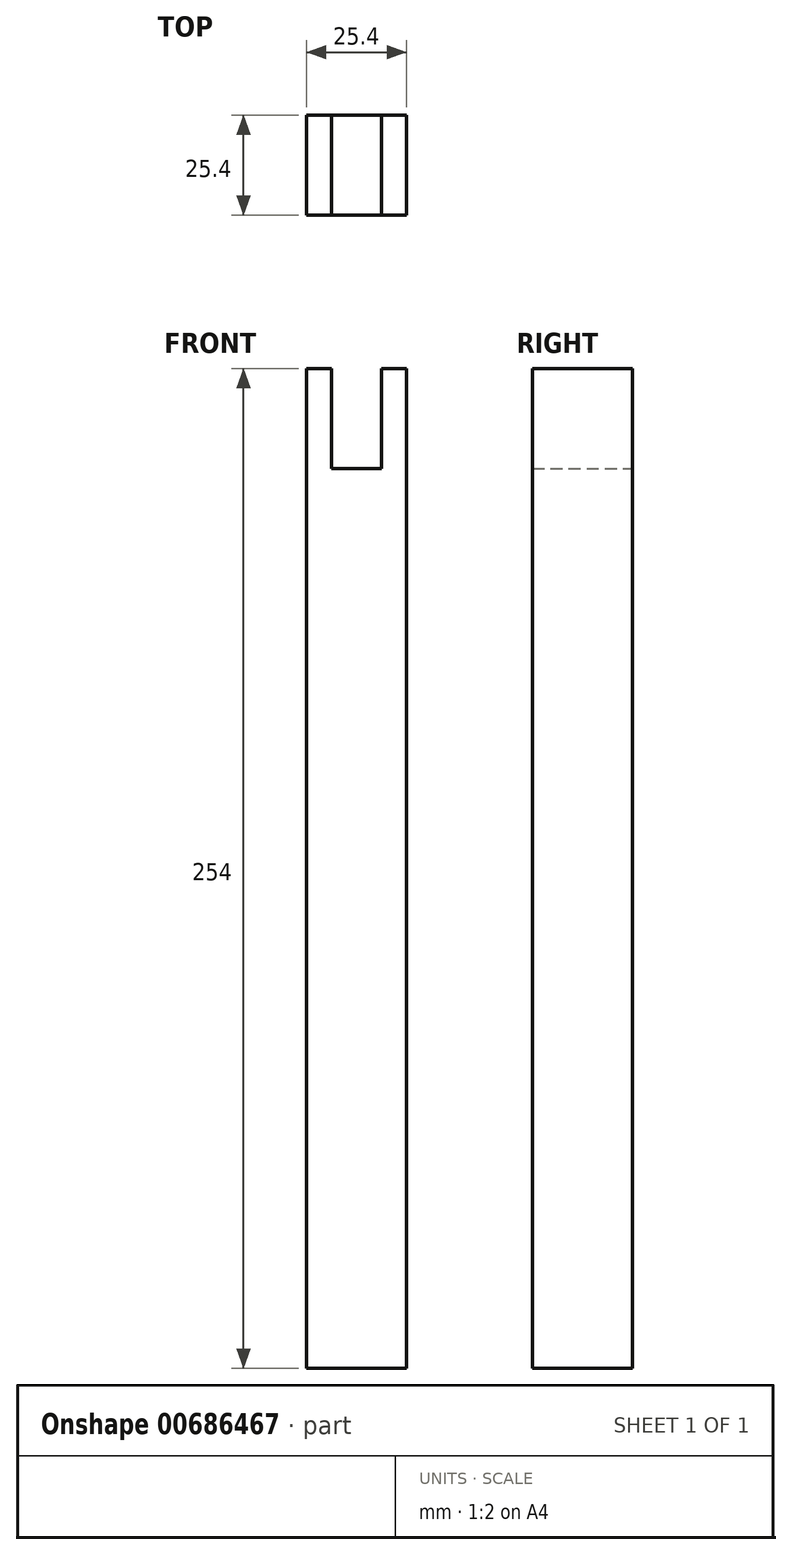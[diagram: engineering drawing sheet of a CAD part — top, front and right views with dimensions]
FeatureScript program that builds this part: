
annotation { "Feature Type Name" : "Feature", "Feature Type Description" : "" }
export const myFeature = defineFeature(function(context is Context, id is Id, definition is map)
    precondition{}
    {
        {
            var Q0;
            Q0=qCreatedBy(makeId("Front.planeOp"),FACE);
            var sketch = newSketch(context, id + "F0", { "sketchPlane" : qUnion([Q0])});
            skLineSegment(sketch, "E0.bottom", {"start": v(0, 0) * mm, "end": v(25.4, 0) * mm});
            skLineSegment(sketch, "E0.top", {"start": v(0, 254) * mm, "end": v(25.4, 254) * mm});
            skLineSegment(sketch, "E0.left", {"start": v(0, 0) * mm, "end": v(0, 254) * mm});
            skLineSegment(sketch, "E0.right", {"start": v(25.4, 0) * mm, "end": v(25.4, 254) * mm});
            skLineSegment(sketch, "E1", {"start": v(19.05, 254) * mm, "end": v(19.05, 228.6) * mm});
            skLineSegment(sketch, "E2", {"start": v(19.05, 228.6) * mm, "end": v(6.35, 228.6) * mm});
            skLineSegment(sketch, "E3", {"start": v(6.35, 228.6) * mm, "end": v(6.35, 254) * mm});
            skSolve(sketch);
        }
        {
            var Q0;
            Q0=makeQuery(id+"F0.imprint","IMPRINT",FACE,{"disambiguationData":[TD([[makeQuery(id+"F0.imprint","IMPRINT",EDGE,{"derivedFrom":sQuery(id+"F0.wireOp",EDGE,"E0.bottom")}),1.0]])]});
            extrude(context, id + "F1", {"entities" : qUnion([Q0]), "depth" : 25.4 * mm, "offsetDistance" : 25.4 * mm});
        }
    });
